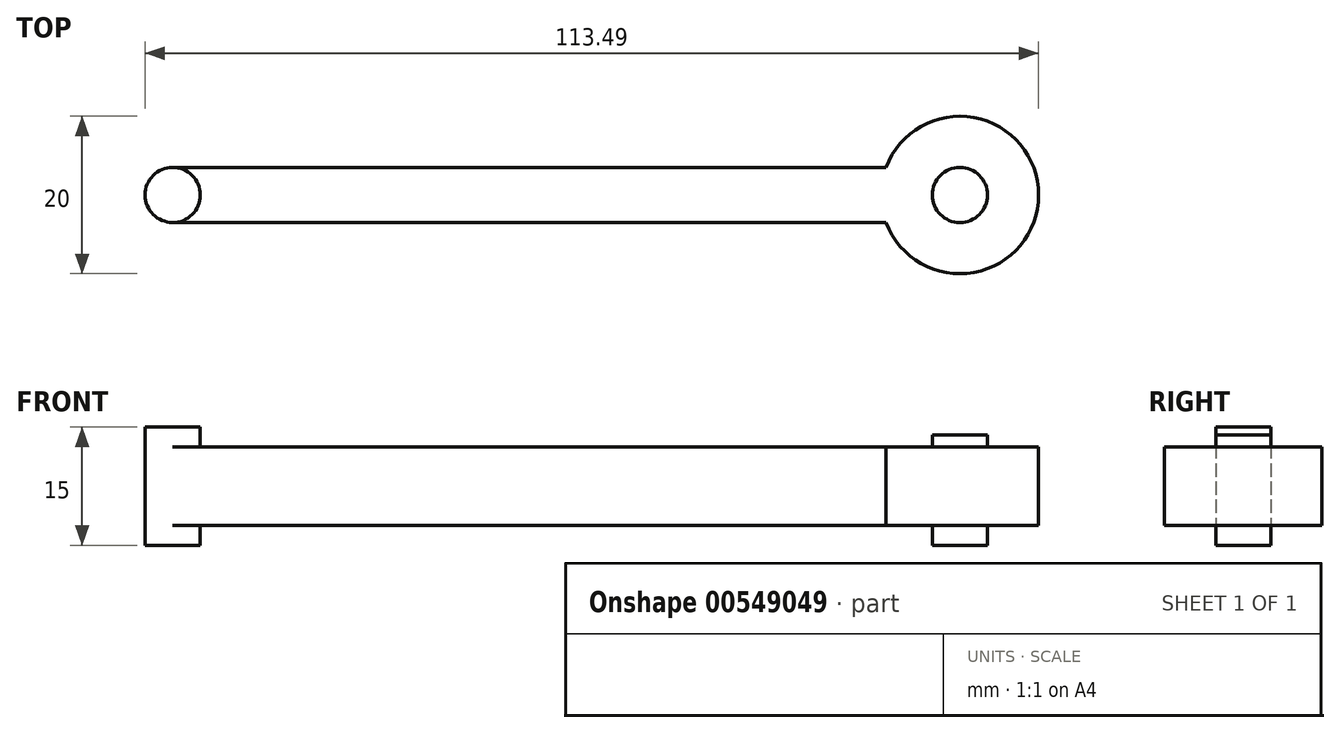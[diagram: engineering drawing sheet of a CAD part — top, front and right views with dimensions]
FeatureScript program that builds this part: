
annotation { "Feature Type Name" : "Feature", "Feature Type Description" : "" }
export const myFeature = defineFeature(function(context is Context, id is Id, definition is map)
    precondition{}
    {
        {
            var Q0;
            Q0=qCreatedBy(makeId("Top.planeOp"),FACE);
            var sketch = newSketch(context, id + "F0", { "sketchPlane" : qUnion([Q0])});
            skCircle(sketch, "E0", {"center": v(-51.13, 12.73) * mm, "radius": 3.5 * mm});
            skCircle(sketch, "E1", {"center": v(-51.13, 12.73) * mm, "radius": 6.25 * mm});
            skLineSegment(sketch, "E2.bottom", {"start": v(-51.14, 16.23) * mm, "end": v(48.86, 16.23) * mm});
            skLineSegment(sketch, "E2.top", {"start": v(-51.14, 9.23) * mm, "end": v(48.86, 9.23) * mm});
            skLineSegment(sketch, "E2.left", {"start": v(-51.14, 16.23) * mm, "end": v(-51.14, 9.23) * mm});
            skLineSegment(sketch, "E2.right", {"start": v(48.86, 16.23) * mm, "end": v(48.86, 9.23) * mm});
            skCircle(sketch, "E3", {"center": v(48.86, 12.73) * mm, "radius": 3.5 * mm});
            skCircle(sketch, "E4", {"center": v(48.86, 12.73) * mm, "radius": 10 * mm});
            skSolve(sketch);
        }
        {
            var Q0;
            {var subQ0=sQuery(id+"F0.wireOp",EDGE,"E2.bottom");var subQ1=sQuery(id+"F0.wireOp",EDGE,"E0");var subQ2=makeQuery(id+"F0.imprint","INTERSECT",VERTEX,{"derivedFrom":[subQ1,subQ0]});Q0=makeQuery(id+"F0.imprint","IMPRINT",FACE,{"disambiguationData":[TD([[makeQuery(id+"F0.imprint","IMPRINT",EDGE,{"disambiguationData":[TD([[subQ2,1.0]])],"derivedFrom":subQ1}),-1.0]])]});}
            var Q1;
            {var subQ0=sQuery(id+"F0.wireOp",EDGE,"E2.bottom");var subQ1=sQuery(id+"F0.wireOp",EDGE,"E1");var subQ2=makeQuery(id+"F0.imprint","INTERSECT",VERTEX,{"derivedFrom":[subQ1,subQ0]});Q1=makeQuery(id+"F0.imprint","IMPRINT",FACE,{"disambiguationData":[TD([[makeQuery(id+"F0.imprint","IMPRINT",EDGE,{"disambiguationData":[TD([[subQ2,1.0]])],"derivedFrom":subQ1}),-1.0]])]});}
            var Q2;
            {var subQ2=sQuery(id+"F0.wireOp",EDGE,"E2.bottom");var subQ4=sQuery(id+"F0.wireOp",EDGE,"E4");var subQ5=makeQuery(id+"F0.imprint","INTERSECT",VERTEX,{"derivedFrom":[subQ2,subQ4]});Q2=makeQuery(id+"F0.imprint","IMPRINT",FACE,{"disambiguationData":[TD([[makeQuery(id+"F0.imprint","IMPRINT",EDGE,{"disambiguationData":[TD([[subQ5,-1.0]])],"derivedFrom":subQ4}),1.0]])]});}
            var Q3;
            {var subQ0=sQuery(id+"F0.wireOp",EDGE,"E2.bottom");var subQ5=sQuery(id+"F0.wireOp",EDGE,"E0");var subQ10=makeQuery(id+"F0.imprint","INTERSECT",VERTEX,{"derivedFrom":[subQ5,subQ0]});Q3=makeQuery(id+"F0.imprint","IMPRINT",FACE,{"disambiguationData":[TD([[makeQuery(id+"F0.imprint","IMPRINT",EDGE,{"disambiguationData":[TD([[subQ10,-1.0]])],"derivedFrom":subQ5}),-1.0]])]});}
            var Q4;
            {var subQ2=sQuery(id+"F0.wireOp",EDGE,"E2.bottom");var subQ4=sQuery(id+"F0.wireOp",EDGE,"E4");var subQ5=makeQuery(id+"F0.imprint","INTERSECT",VERTEX,{"derivedFrom":[subQ2,subQ4]});Q4=makeQuery(id+"F0.imprint","IMPRINT",FACE,{"disambiguationData":[TD([[makeQuery(id+"F0.imprint","IMPRINT",EDGE,{"disambiguationData":[TD([[subQ5,1.0]])],"derivedFrom":subQ4}),1.0]])]});}
            extrude(context, id + "F1", {"entities" : qUnion([Q0, Q1, Q2, Q3, Q4]), "endBound" : BoundingType.SYMMETRIC, "depth" : 10 * mm, "offsetDistance" : 25 * mm});
        }
        {
            var Q0;
            {var subQ0=sQuery(id+"F0.wireOp",EDGE,"E2.left");Q0=makeQuery(id+"F0.imprint","IMPRINT",FACE,{"disambiguationData":[TD([[makeQuery(id+"F0.imprint","IMPRINT",EDGE,{"derivedFrom":subQ0}),-1.0]])]});}
            var Q1;
            {var subQ2=sQuery(id+"F0.wireOp",EDGE,"E2.left");Q1=makeQuery(id+"F0.imprint","IMPRINT",FACE,{"disambiguationData":[TD([[makeQuery(id+"F0.imprint","IMPRINT",EDGE,{"derivedFrom":subQ2}),1.0]])]});}
            extrude(context, id + "F2", {"entities" : qUnion([Q0, Q1]), "operationType" : NewBodyOperationType.ADD, "endBound" : BoundingType.SYMMETRIC, "depth" : 15 * mm, "offsetDistance" : 25 * mm});
        }
        {
            var Q0;
            {var subQ0=sQuery(id+"F0.wireOp",EDGE,"E2.right");Q0=makeQuery(id+"F0.imprint","IMPRINT",FACE,{"disambiguationData":[TD([[makeQuery(id+"F0.imprint","IMPRINT",EDGE,{"derivedFrom":subQ0}),1.0]])]});}
            var Q1;
            {var subQ0=sQuery(id+"F0.wireOp",EDGE,"E2.right");Q1=makeQuery(id+"F0.imprint","IMPRINT",FACE,{"disambiguationData":[TD([[makeQuery(id+"F0.imprint","IMPRINT",EDGE,{"derivedFrom":subQ0}),-1.0]])]});}
            extrude(context, id + "F3", {"entities" : qUnion([Q0, Q1]), "operationType" : NewBodyOperationType.ADD, "oppositeDirection" : true, "depth" : 7.5 * mm, "offsetDistance" : 25 * mm});
        }
        {
            var Q0;
            {var subQ0=sQuery(id+"F0.wireOp",EDGE,"E2.right");Q0=makeQuery(id+"F0.imprint","IMPRINT",FACE,{"disambiguationData":[TD([[makeQuery(id+"F0.imprint","IMPRINT",EDGE,{"derivedFrom":subQ0}),1.0]])]});}
            var Q1;
            {var subQ0=sQuery(id+"F0.wireOp",EDGE,"E2.right");Q1=makeQuery(id+"F0.imprint","IMPRINT",FACE,{"disambiguationData":[TD([[makeQuery(id+"F0.imprint","IMPRINT",EDGE,{"derivedFrom":subQ0}),-1.0]])]});}
            extrude(context, id + "F4", {"entities" : qUnion([Q0, Q1]), "operationType" : NewBodyOperationType.ADD, "depth" : 6.5 * mm, "offsetDistance" : 25 * mm});
        }
    });
